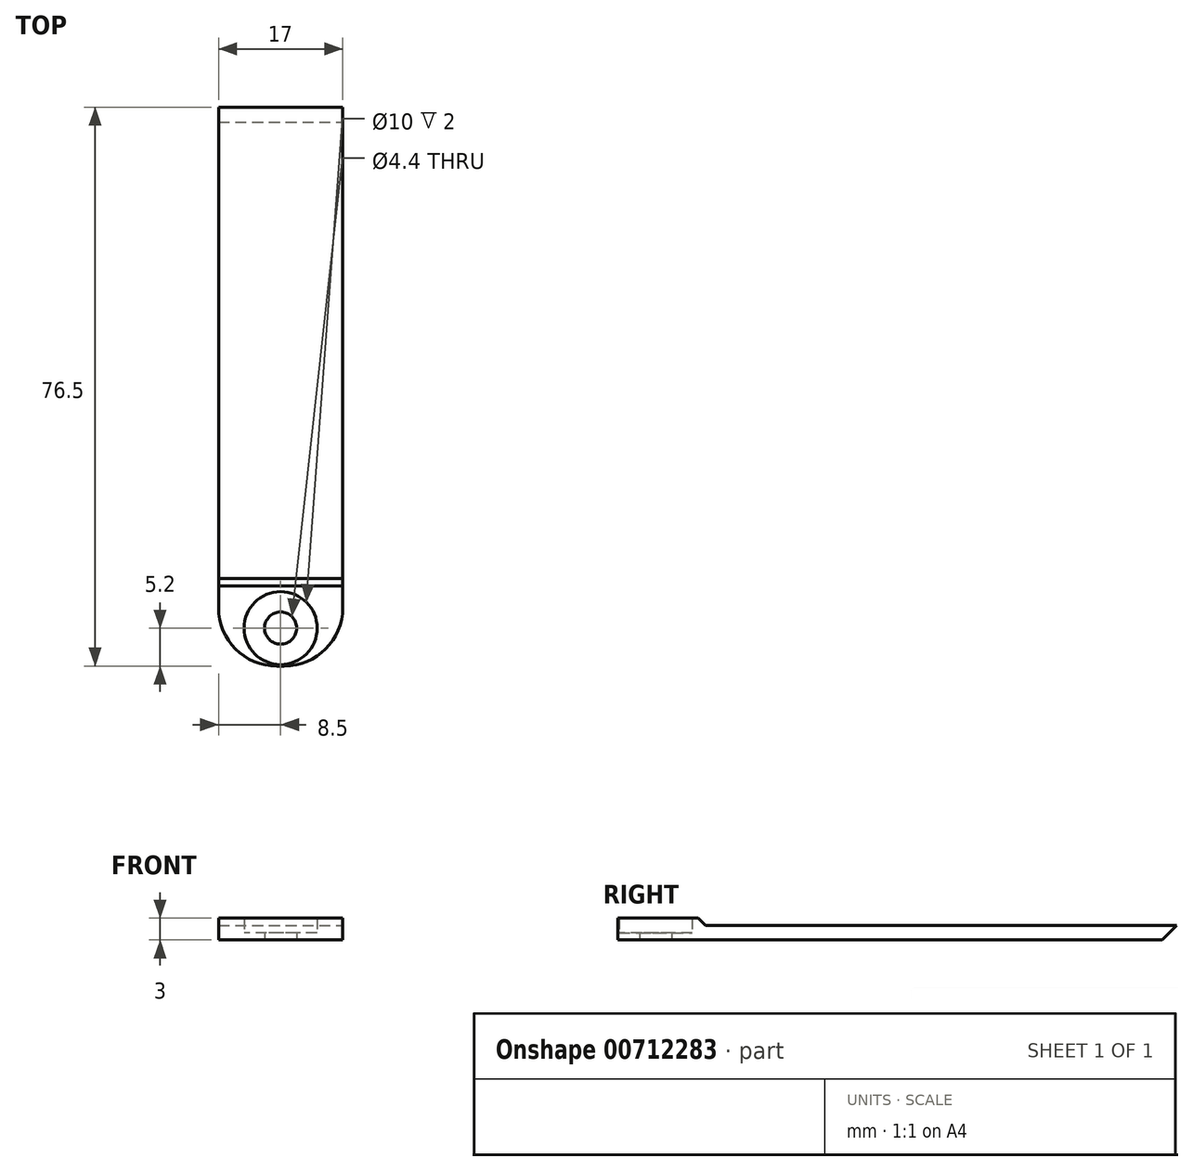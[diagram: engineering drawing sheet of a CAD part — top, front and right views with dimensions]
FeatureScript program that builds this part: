
annotation { "Feature Type Name" : "Feature", "Feature Type Description" : "" }
export const myFeature = defineFeature(function(context is Context, id is Id, definition is map)
    precondition{}
    {
        {
            var Q0;
            Q0=qCreatedBy(makeId("Top.planeOp"),FACE);
            var sketch = newSketch(context, id + "F0", { "sketchPlane" : qUnion([Q0])});
            skLineSegment(sketch, "E0.bottom", {"start": v(-8.5, 38.25) * mm, "end": v(8.5, 38.25) * mm});
            skLineSegment(sketch, "E0.top", {"start": v(-8.5, -38.25) * mm, "end": v(8.5, -38.25) * mm});
            skLineSegment(sketch, "E0.left", {"start": v(-8.5, 38.25) * mm, "end": v(-8.5, -38.25) * mm});
            skLineSegment(sketch, "E0.right", {"start": v(8.5, 38.25) * mm, "end": v(8.5, -38.25) * mm});
            skPoint(sketch, "E0.middle", {"position": v(0, 0) * mm});
            skCircle(sketch, "E1", {"center": v(0, -33.05) * mm, "radius": 5 * mm});
            skLineSegment(sketch, "E2", {"start": v(8.5, -26.25) * mm, "end": v(-8.5, -26.25) * mm});
            skCircle(sketch, "E3", {"center": v(0, -33.05) * mm, "radius": 2.2 * mm});
            skSolve(sketch);
        }
        {
            var Q0;
            Q0=makeQuery(id+"F0.imprint","IMPRINT",FACE,{"disambiguationData":[TD([[makeQuery(id+"F0.imprint","IMPRINT",EDGE,{"derivedFrom":sQuery(id+"F0.wireOp",EDGE,"E0.bottom")}),-1.0]])]});
            var Q1;
            {var subQ1=sQuery(id+"F0.wireOp",EDGE,"E0.top");Q1=makeQuery(id+"F0.imprint","IMPRINT",FACE,{"disambiguationData":[TD([[makeQuery(id+"F0.imprint","IMPRINT",EDGE,{"derivedFrom":subQ1}),1.0]])]});}
            extrude(context, id + "F1", {"entities" : qUnion([Q0, Q1]), "depth" : 2 * mm, "offsetDistance" : 25 * mm});
        }
        {
            var Q0;
            Q0=makeQuery(id+"F1.opExtrude","SWEPT_EDGE",EDGE,{"disambiguationData":[OSD([sQuery(id+"F0.wireOp",EDGE,"E0.top"),sQuery(id+"F0.wireOp",EDGE,"E0.right")])]});
            var Q1;
            Q1=makeQuery(id+"F1.opExtrude","SWEPT_EDGE",EDGE,{"disambiguationData":[OSD([sQuery(id+"F0.wireOp",EDGE,"E0.top"),sQuery(id+"F0.wireOp",EDGE,"E0.left")])]});
            fillet(context, id + "F2", {"entities" : qUnion([Q0, Q1]), "radius" : 8 * mm, "tangentPropagation" : true, "allowEdgeOverflow" : false});
        }
        {
            var Q0;
            Q0=makeQuery(id+"F1.opExtrude","CAP_EDGE",EDGE,{"disambiguationData":[OSD([sQuery(id+"F0.wireOp",EDGE,"E0.bottom")])],"isStart":true});
            chamfer(context, id + "F3", {"entities" : qUnion([Q0]), "width" : 2 * mm, "tangentPropagation" : true});
        }
        {
            var Q0;
            Q0=makeQuery(id+"F0.imprint","IMPRINT",FACE,{"disambiguationData":[TD([[makeQuery(id+"F0.imprint","IMPRINT",EDGE,{"derivedFrom":sQuery(id+"F0.wireOp",EDGE,"E1")}),1.0]])]});
            extrude(context, id + "F4", {"entities" : qUnion([Q0]), "operationType" : NewBodyOperationType.ADD, "depth" : 1 * mm, "offsetDistance" : 25 * mm});
        }
        {
            var Q0;
            {var subQ1=sQuery(id+"F0.wireOp",EDGE,"E0.top");Q0=makeQuery(id+"F0.imprint","IMPRINT",FACE,{"disambiguationData":[TD([[makeQuery(id+"F0.imprint","IMPRINT",EDGE,{"derivedFrom":subQ1}),1.0]])]});}
            extrude(context, id + "F5", {"entities" : qUnion([Q0]), "operationType" : NewBodyOperationType.ADD, "depth" : 3 * mm, "offsetDistance" : 25 * mm});
        }
        {
            var Q0;
            Q0=makeQuery(id+"F5.opExtrude","SWEPT_EDGE",EDGE,{"disambiguationData":[OSD([sQuery(id+"F0.wireOp",EDGE,"E0.top"),sQuery(id+"F0.wireOp",EDGE,"E0.right")])]});
            var Q1;
            Q1=makeQuery(id+"F5.opExtrude","SWEPT_EDGE",EDGE,{"disambiguationData":[OSD([sQuery(id+"F0.wireOp",EDGE,"E0.top"),sQuery(id+"F0.wireOp",EDGE,"E0.left")])]});
            fillet(context, id + "F6", {"entities" : qUnion([Q0, Q1]), "radius" : 8 * mm, "tangentPropagation" : true, "allowEdgeOverflow" : false});
        }
        {
            var Q0;
            Q0=makeQuery(id+"F5.opExtrude","CAP_EDGE",EDGE,{"disambiguationData":[OSD([sQuery(id+"F0.wireOp",EDGE,"E2")])],"isStart":false});
            chamfer(context, id + "F7", {"entities" : qUnion([Q0]), "width" : 1 * mm, "tangentPropagation" : true});
        }
    });
